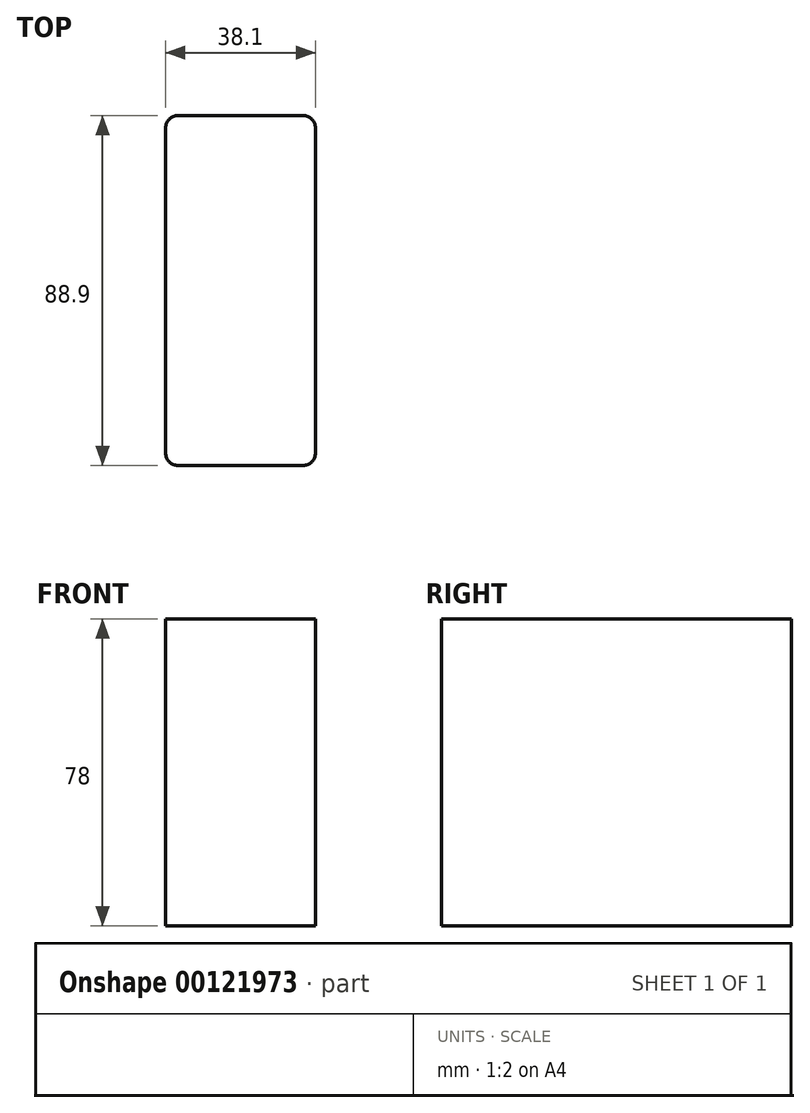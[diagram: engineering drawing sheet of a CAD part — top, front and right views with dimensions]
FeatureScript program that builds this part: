
annotation { "Feature Type Name" : "Feature", "Feature Type Description" : "" }
export const myFeature = defineFeature(function(context is Context, id is Id, definition is map)
    precondition{}
    {
        {
            var Q0;
            Q0=qCreatedBy(makeId("Top.planeOp"),FACE);
            var sketch = newSketch(context, id + "F0", { "sketchPlane" : qUnion([Q0])});
            skLineSegment(sketch, "E0.bottom", {"start": v(3.18, 0) * mm, "end": v(34.93, 0) * mm});
            skLineSegment(sketch, "E0.top", {"start": v(3.18, 88.9) * mm, "end": v(34.92, 88.9) * mm});
            skLineSegment(sketch, "E0.left", {"start": v(0, 3.18) * mm, "end": v(0, 85.73) * mm});
            skLineSegment(sketch, "E0.right", {"start": v(38.1, 3.18) * mm, "end": v(38.1, 85.73) * mm});
            skPoint(sketch, "E1.visualSharp", {"position": v(38.1, 0) * mm});
            skArc(sketch, "E1.filletArc", {"start": v(34.93, 0) * mm, "mid": v(37.17, 0.93) * mm, "end": v(38.1, 3.18) * mm});
            skPoint(sketch, "E2.visualSharp", {"position": v(38.1, 88.9) * mm});
            skArc(sketch, "E2.filletArc", {"start": v(38.1, 85.73) * mm, "mid": v(37.17, 87.97) * mm, "end": v(34.92, 88.9) * mm});
            skPoint(sketch, "E3.visualSharp", {"position": v(0, 88.9) * mm});
            skArc(sketch, "E3.filletArc", {"start": v(3.18, 88.9) * mm, "mid": v(0.93, 87.97) * mm, "end": v(0, 85.73) * mm});
            skPoint(sketch, "E4.visualSharp", {"position": v(0, 0) * mm});
            skArc(sketch, "E4.filletArc", {"start": v(0, 3.18) * mm, "mid": v(0.93, 0.93) * mm, "end": v(3.18, 0) * mm});
            skSolve(sketch);
        }
        {
            assignVariable(context, id + "F1", {"name" : "Length", "anyValue" : 78});
        }
        {
            var Q0;
            Q0=qSketchRegion(id+"F0",true);
            extrude(context, id + "F2", {"entities" : qUnion([Q0]), "depth" : (getVariable(context, 'Length')) * mm});
        }
    });
